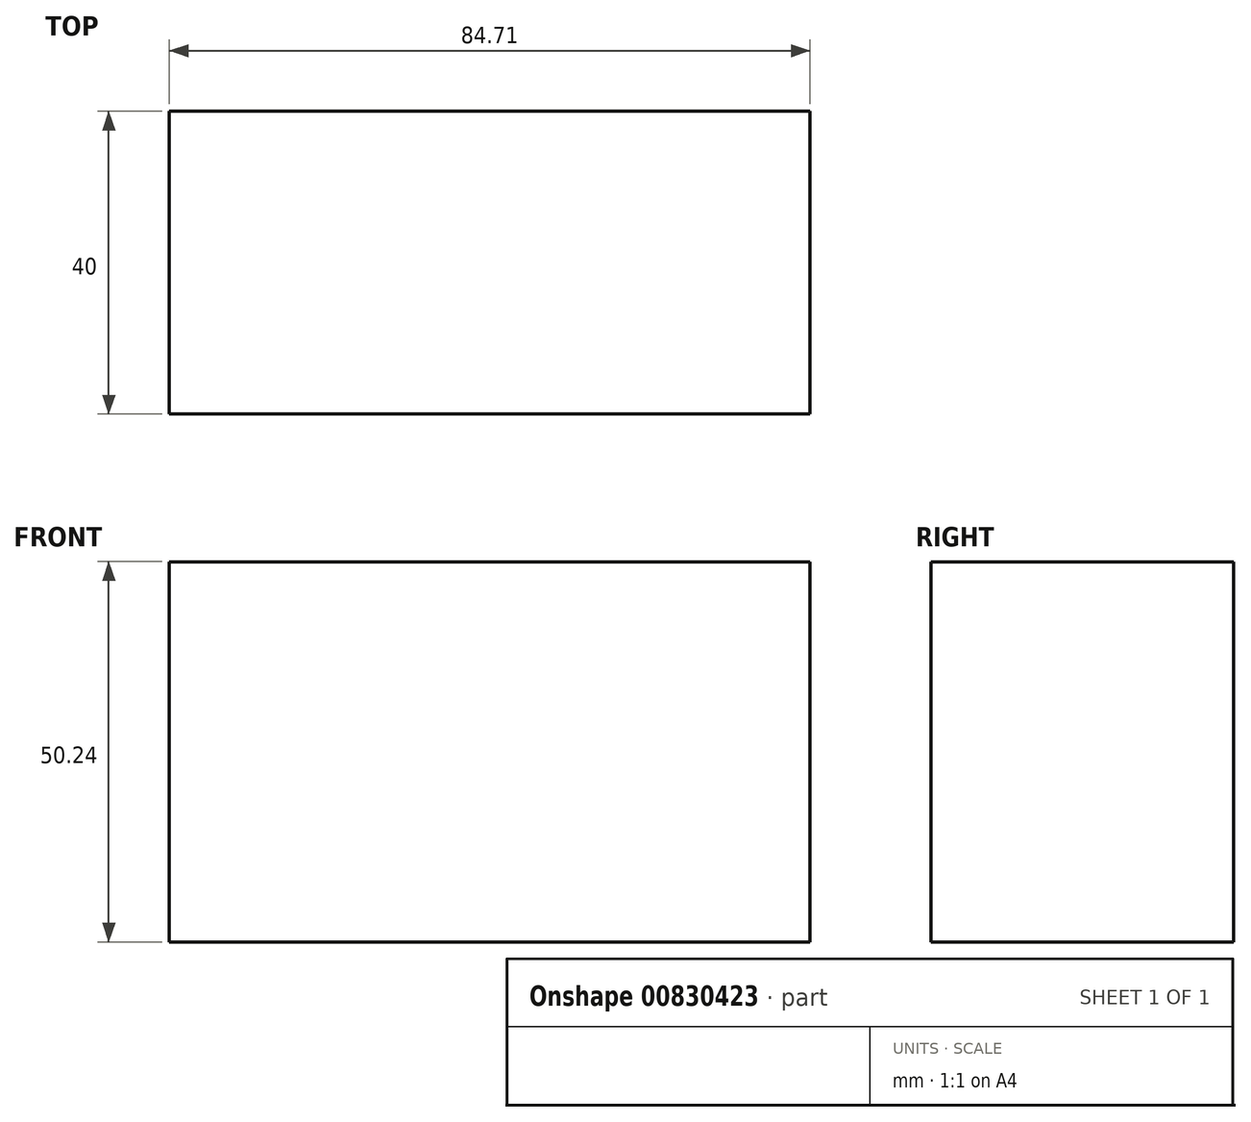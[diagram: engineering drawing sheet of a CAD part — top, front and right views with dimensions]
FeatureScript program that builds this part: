
annotation { "Feature Type Name" : "Feature", "Feature Type Description" : "" }
export const myFeature = defineFeature(function(context is Context, id is Id, definition is map)
    precondition{}
    {
        {
            var Q0;
            Q0=qCreatedBy(makeId("Front.planeOp"),FACE);
            var sketch = newSketch(context, id + "F0", { "sketchPlane" : qUnion([Q0])});
            skLineSegment(sketch, "E0.bottom", {"start": v(0, 0) * mm, "end": v(84.71, 0) * mm});
            skLineSegment(sketch, "E0.top", {"start": v(0, 50.24) * mm, "end": v(84.71, 50.24) * mm});
            skLineSegment(sketch, "E0.left", {"start": v(0, 0) * mm, "end": v(0, 50.24) * mm});
            skLineSegment(sketch, "E0.right", {"start": v(84.71, 0) * mm, "end": v(84.71, 50.24) * mm});
            skSolve(sketch);
        }
        {
            var Q0;
            Q0=makeQuery(id+"F0.imprint","IMPRINT",FACE,{"disambiguationData":[TD([[makeQuery(id+"F0.imprint","IMPRINT",EDGE,{"derivedFrom":sQuery(id+"F0.wireOp",EDGE,"E0.bottom")}),1.0]])]});
            extrude(context, id + "F1", {"entities" : qUnion([Q0]), "depth" : 40 * mm, "offsetDistance" : 25.4 * mm});
        }
    });
